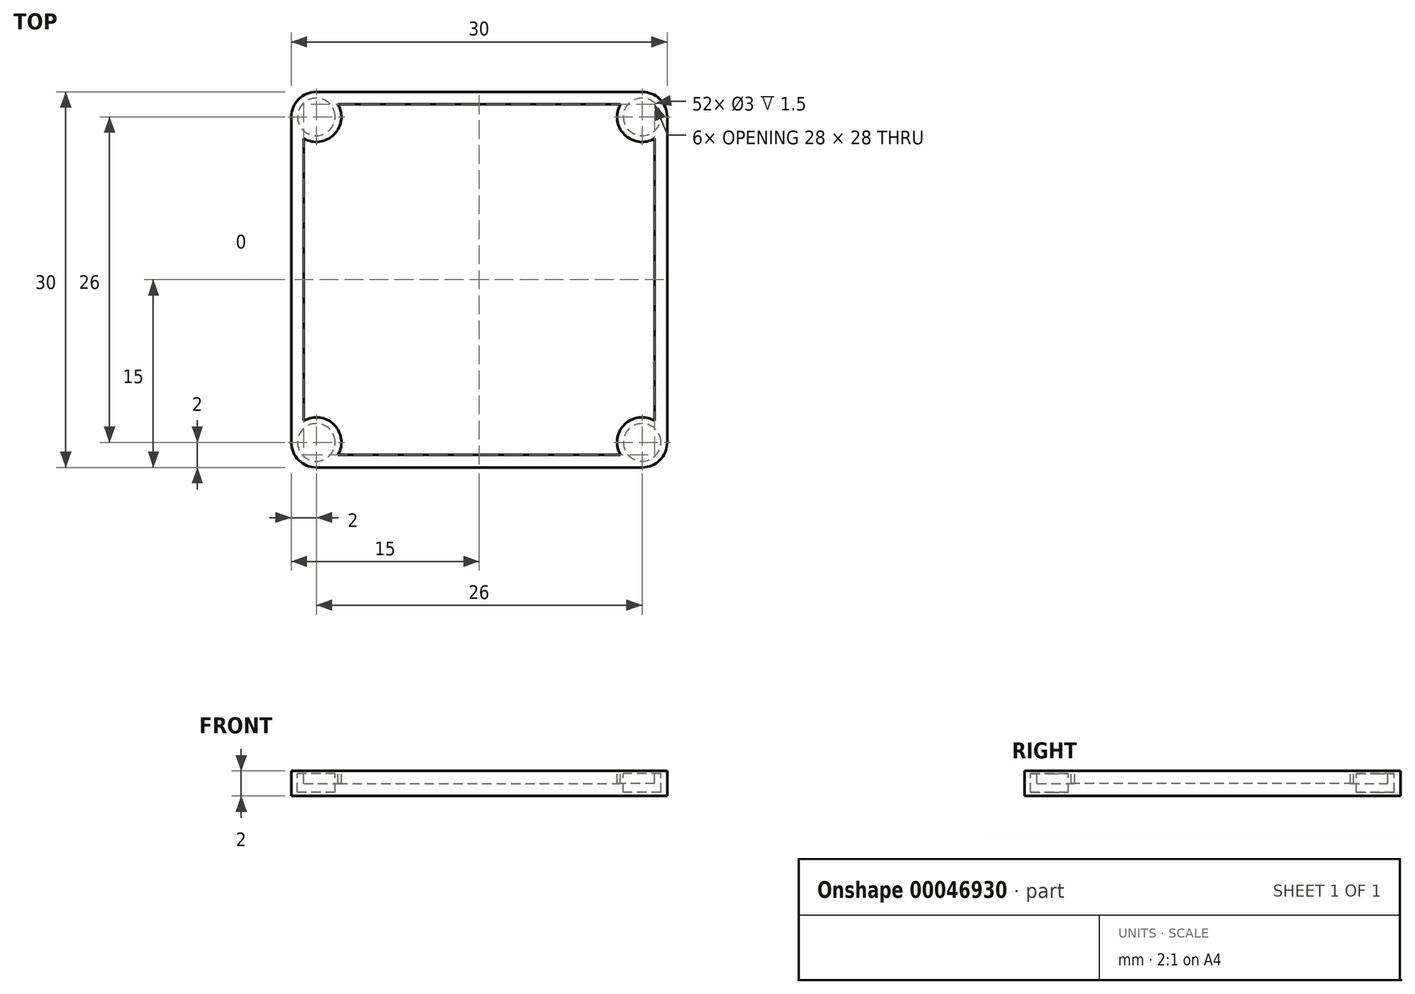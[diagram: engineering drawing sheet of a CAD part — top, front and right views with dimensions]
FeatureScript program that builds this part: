
annotation { "Feature Type Name" : "Feature", "Feature Type Description" : "" }
export const myFeature = defineFeature(function(context is Context, id is Id, definition is map)
    precondition{}
    {
        {
            var Q0;
            Q0=qCreatedBy(makeId("Top.planeOp"),FACE);
            var sketch = newSketch(context, id + "F0", { "sketchPlane" : qUnion([Q0])});
            skLineSegment(sketch, "E0.rect.bottom", {"start": v(-15, 15) * mm, "end": v(15, 15) * mm});
            skLineSegment(sketch, "E0.rect.top", {"start": v(-15, -15) * mm, "end": v(15, -15) * mm});
            skLineSegment(sketch, "E0.rect.left", {"start": v(-15, 15) * mm, "end": v(-15, -15) * mm});
            skLineSegment(sketch, "E0.rect.right", {"start": v(15, 15) * mm, "end": v(15, -15) * mm});
            skPoint(sketch, "E0.rect.middle", {"position": v(0, 0) * mm});
            skSolve(sketch);
        }
        {
            var Q0;
            Q0=qSketchRegion(id+"F0",true);
            extrude(context, id + "F1", {"entities" : qUnion([Q0]), "depth" : 2 * mm});
        }
        {
            var Q0;
            Q0=makeQuery(id+"F1.opExtrude","CAP_FACE",FACE,{"disambiguationData":[OSD([sQuery(id+"F0.wireOp",EDGE,"E0.rect.bottom"),sQuery(id+"F0.wireOp",EDGE,"E0.rect.top"),sQuery(id+"F0.wireOp",EDGE,"E0.rect.left"),sQuery(id+"F0.wireOp",EDGE,"E0.rect.right")])],"isStart":false});
            var sketch = newSketch(context, id + "F2", { "sketchPlane" : qUnion([Q0])});
            skLineSegment(sketch, "E1.0", {"start": v(-15, 15) * mm, "end": v(15, 15) * mm, "construction": true});
            skLineSegment(sketch, "E2.0", {"start": v(-15, 15) * mm, "end": v(-15, -15) * mm, "construction": true});
            skLineSegment(sketch, "E3.0", {"start": v(-15, -15) * mm, "end": v(15, -15) * mm, "construction": true});
            skLineSegment(sketch, "E4.0", {"start": v(15, 15) * mm, "end": v(15, -15) * mm, "construction": true});
            skArc(sketch, "E5", {"start": v(-14, 11.27) * mm, "mid": v(-11.59, 11.59) * mm, "end": v(-11.27, 14) * mm});
            skArc(sketch, "E6.MirrorC", {"start": v(14, 11.27) * mm, "mid": v(11.59, 11.59) * mm, "end": v(11.27, 14) * mm});
            skArc(sketch, "E7.MirrorC", {"start": v(-14, -11.27) * mm, "mid": v(-11.59, -11.59) * mm, "end": v(-11.27, -14) * mm});
            skArc(sketch, "E8.MirrorC", {"start": v(14, -11.27) * mm, "mid": v(11.59, -11.59) * mm, "end": v(11.27, -14) * mm});
            skLineSegment(sketch, "E9", {"start": v(-11.27, 14) * mm, "end": v(11.27, 14) * mm});
            skLineSegment(sketch, "E10.MirrorCS", {"start": v(-11.27, -14) * mm, "end": v(11.27, -14) * mm});
            skLineSegment(sketch, "E11", {"start": v(-14, 11.27) * mm, "end": v(-14, -11.27) * mm});
            skLineSegment(sketch, "E12.MirrorCS", {"start": v(14, 11.27) * mm, "end": v(14, -11.27) * mm});
            skSolve(sketch);
        }
        {
            var Q0;
            Q0=qSketchRegion(id+"F2",true);
            extrude(context, id + "F3", {"entities" : qUnion([Q0]), "operationType" : NewBodyOperationType.REMOVE, "oppositeDirection" : true, "depth" : 1 * mm});
        }
        {
            var Q0;
            Q0=makeQuery(id+"F1.opExtrude","CAP_FACE",FACE,{"disambiguationData":[OSD([sQuery(id+"F0.wireOp",EDGE,"E0.rect.bottom"),sQuery(id+"F0.wireOp",EDGE,"E0.rect.top"),sQuery(id+"F0.wireOp",EDGE,"E0.rect.left"),sQuery(id+"F0.wireOp",EDGE,"E0.rect.right")])],"isStart":false});
            cPlane(context, id + "F4", {"entities" : qUnion([Q0]), "cplaneType" : CPlaneType.OFFSET, "offset" : 0.2 * mm, "oppositeDirection" : true, "width" : 150 * mm, "height" : 150 * mm});
        }
        {
            var Q0;
            Q0=qCreatedBy(id+"F4.planeOp",FACE);
            var sketch = newSketch(context, id + "F5", { "sketchPlane" : qUnion([Q0])});
            skPoint(sketch, "E13.0", {"position": v(-13, 13) * mm});
            skCircle(sketch, "E14", {"center": v(-13, 13) * mm, "radius": 1.5 * mm});
            skCircle(sketch, "E15.MirrorC", {"center": v(13, 13) * mm, "radius": 1.5 * mm});
            skCircle(sketch, "E16.MirrorC", {"center": v(-13, -13) * mm, "radius": 1.5 * mm});
            skCircle(sketch, "E17.MirrorC", {"center": v(13, -13) * mm, "radius": 1.5 * mm});
            skSolve(sketch);
        }
        {
            var Q0;
            Q0=qSketchRegion(id+"F5",true);
            extrude(context, id + "F6", {"entities" : qUnion([Q0]), "operationType" : NewBodyOperationType.REMOVE, "oppositeDirection" : true, "depth" : 1.5 * mm});
        }
        {
            var Q0;
            Q0=makeQuery(id+"F1.opExtrude","SWEPT_EDGE",EDGE,{"disambiguationData":[OSD([sQuery(id+"F0.wireOp",EDGE,"E0.rect.bottom"),sQuery(id+"F0.wireOp",EDGE,"E0.rect.left")])]});
            var Q1;
            Q1=makeQuery(id+"F1.opExtrude","SWEPT_EDGE",EDGE,{"disambiguationData":[OSD([sQuery(id+"F0.wireOp",EDGE,"E0.rect.top"),sQuery(id+"F0.wireOp",EDGE,"E0.rect.left")])]});
            var Q2;
            Q2=makeQuery(id+"F1.opExtrude","SWEPT_EDGE",EDGE,{"disambiguationData":[OSD([sQuery(id+"F0.wireOp",EDGE,"E0.rect.top"),sQuery(id+"F0.wireOp",EDGE,"E0.rect.right")])]});
            var Q3;
            Q3=makeQuery(id+"F1.opExtrude","SWEPT_EDGE",EDGE,{"disambiguationData":[OSD([sQuery(id+"F0.wireOp",EDGE,"E0.rect.bottom"),sQuery(id+"F0.wireOp",EDGE,"E0.rect.right")])]});
            fillet(context, id + "F7", {"entities" : qUnion([Q0, Q1, Q2, Q3]), "radius" : 2 * mm, "tangentPropagation" : true, "allowEdgeOverflow" : false});
        }
    });
